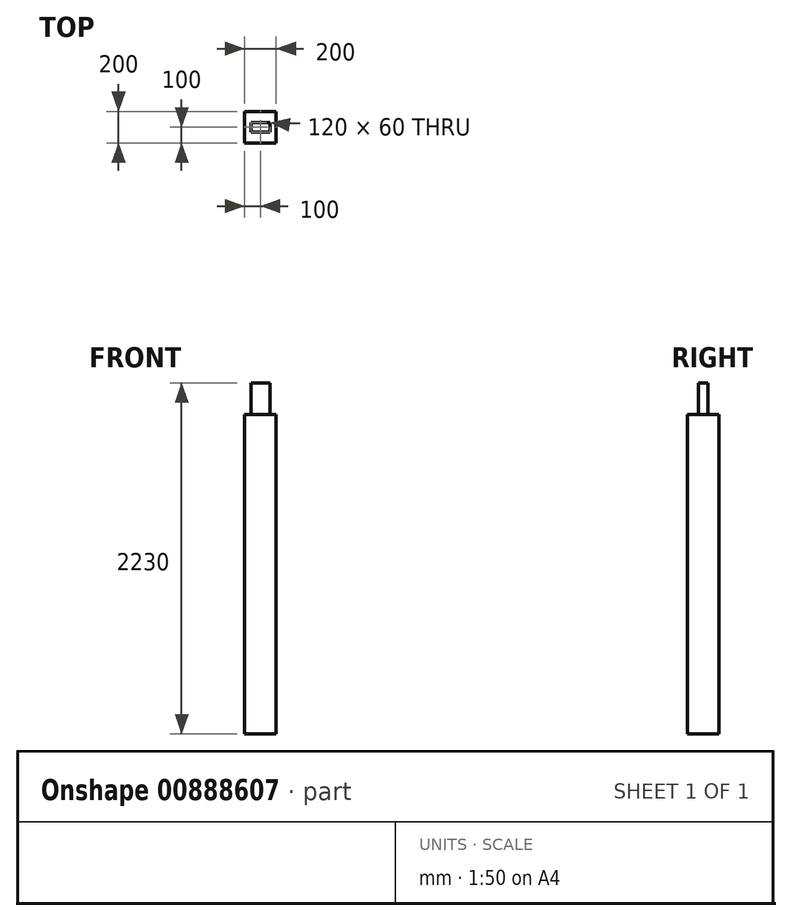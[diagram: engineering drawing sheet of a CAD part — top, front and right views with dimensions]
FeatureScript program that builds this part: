
annotation { "Feature Type Name" : "Feature", "Feature Type Description" : "" }
export const myFeature = defineFeature(function(context is Context, id is Id, definition is map)
    precondition{}
    {
        {
            var Q0;
            Q0=qCreatedBy(makeId("Top.planeOp"),FACE);
            var sketch = newSketch(context, id + "F0", { "sketchPlane" : qUnion([Q0])});
            skLineSegment(sketch, "E0.bottom", {"start": v(0, 0) * mm, "end": v(200, 0) * mm});
            skLineSegment(sketch, "E0.top", {"start": v(0, 200) * mm, "end": v(200, 200) * mm});
            skLineSegment(sketch, "E0.left", {"start": v(0, 0) * mm, "end": v(0, 200) * mm});
            skLineSegment(sketch, "E0.right", {"start": v(200, 0) * mm, "end": v(200, 200) * mm});
            skSolve(sketch);
        }
        {
            var Q0;
            Q0=makeQuery(id+"F0.imprint","IMPRINT",FACE,{"disambiguationData":[TD([[makeQuery(id+"F0.imprint","IMPRINT",EDGE,{"derivedFrom":sQuery(id+"F0.wireOp",EDGE,"E0.bottom")}),1.0]])]});
            extrude(context, id + "F1", {"entities" : qUnion([Q0]), "depth" : (2600 - 370) * mm, "offsetDistance" : 25 * mm});
        }
        {
            var Q0;
            Q0=makeQuery(id+"F1.opExtrude","CAP_FACE",FACE,{"disambiguationData":[OSD([sQuery(id+"F0.wireOp",EDGE,"E0.bottom"),sQuery(id+"F0.wireOp",EDGE,"E0.top"),sQuery(id+"F0.wireOp",EDGE,"E0.left"),sQuery(id+"F0.wireOp",EDGE,"E0.right")])],"isStart":false});
            var sketch = newSketch(context, id + "F2", { "sketchPlane" : qUnion([Q0])});
            skLineSegment(sketch, "E1.bottom", {"start": v(0, 0) * mm, "end": v(200, 0) * mm});
            skLineSegment(sketch, "E1.top", {"start": v(0, 200) * mm, "end": v(200, 200) * mm});
            skLineSegment(sketch, "E1.left", {"start": v(0, 0) * mm, "end": v(0, 200) * mm});
            skLineSegment(sketch, "E1.right", {"start": v(200, 0) * mm, "end": v(200, 200) * mm});
            skLineSegment(sketch, "E2.bottom", {"start": v(160, 70) * mm, "end": v(40, 70) * mm});
            skLineSegment(sketch, "E2.top", {"start": v(160, 130) * mm, "end": v(40, 130) * mm});
            skLineSegment(sketch, "E2.left", {"start": v(160, 70) * mm, "end": v(160, 130) * mm});
            skLineSegment(sketch, "E2.right", {"start": v(40, 70) * mm, "end": v(40, 130) * mm});
            skLineSegment(sketch, "E3", {"start": v(200, 100) * mm, "end": v(0, 100) * mm, "construction": true});
            skPoint(sketch, "E3.endSnap0", {"position": v(40, 100) * mm});
            skLineSegment(sketch, "E4", {"start": v(100, 0) * mm, "end": v(100, 200) * mm, "construction": true});
            skPoint(sketch, "E4.endSnap0", {"position": v(100, 70) * mm});
            skSolve(sketch);
        }
        {
            var Q0;
            Q0=makeQuery(id+"F2.imprint","IMPRINT",FACE,{"disambiguationData":[TD([[makeQuery(id+"F2.imprint","IMPRINT",EDGE,{"derivedFrom":sQuery(id+"F2.wireOp",EDGE,"E1.bottom")}),1.0]])]});
            extrude(context, id + "F3", {"entities" : qUnion([Q0]), "operationType" : NewBodyOperationType.REMOVE, "oppositeDirection" : true, "depth" : 200 * mm, "offsetDistance" : 25 * mm});
        }
    });
